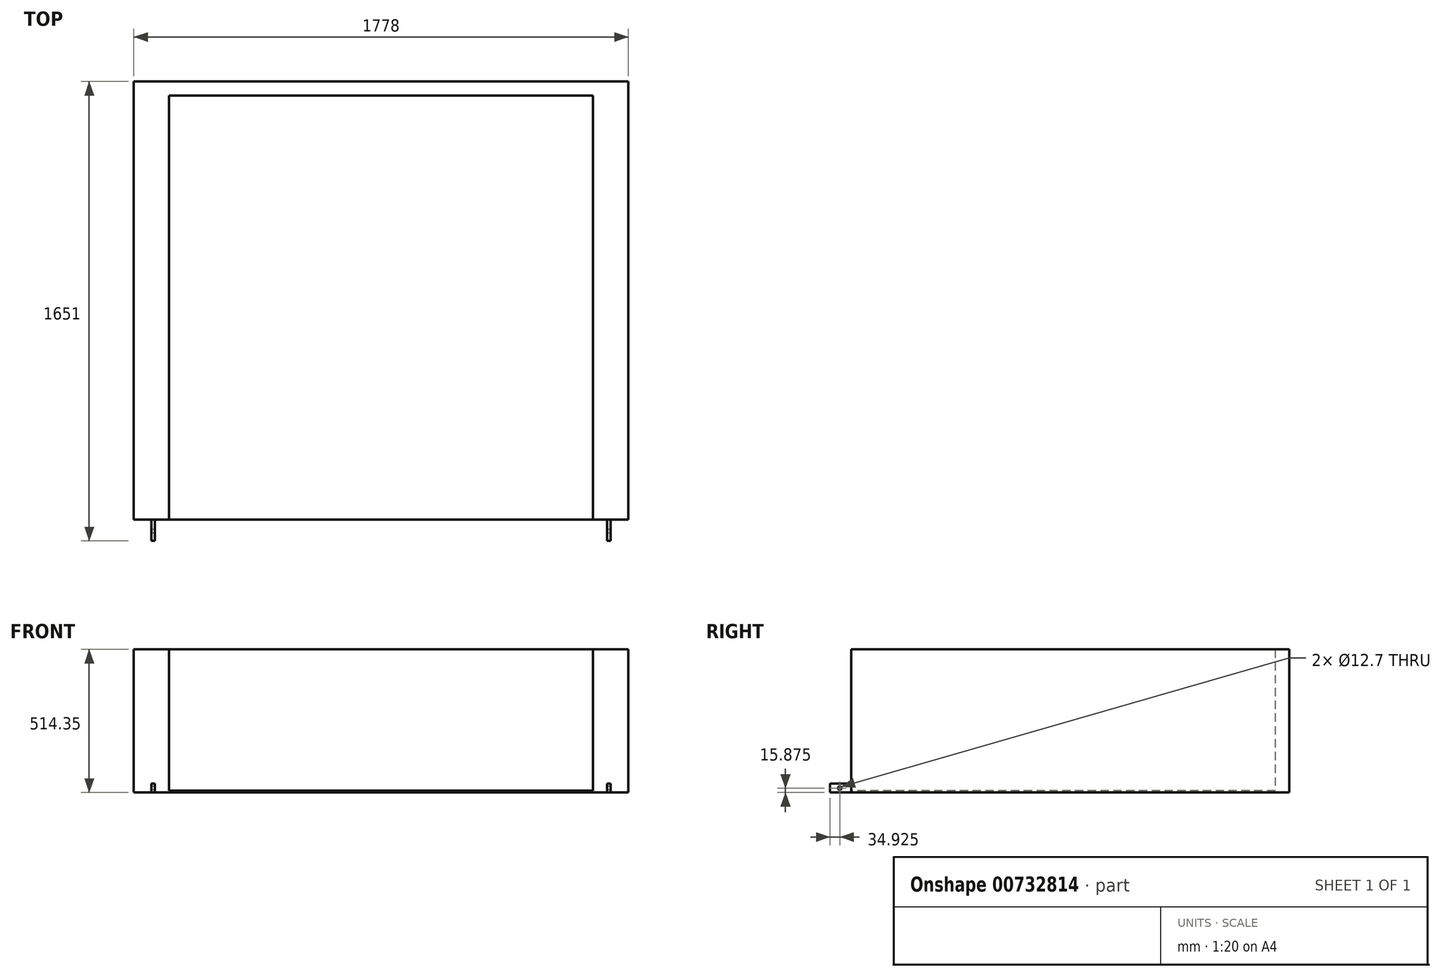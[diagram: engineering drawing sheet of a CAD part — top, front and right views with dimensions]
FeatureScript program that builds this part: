
annotation { "Feature Type Name" : "Feature", "Feature Type Description" : "" }
export const myFeature = defineFeature(function(context is Context, id is Id, definition is map)
    precondition{}
    {
        {
            var Q0;
            Q0=qCreatedBy(makeId("Top.planeOp"),FACE);
            var sketch = newSketch(context, id + "F0", { "sketchPlane" : qUnion([Q0])});
            skLineSegment(sketch, "E0.bottom", {"start": v(-889, 787.4) * mm, "end": v(889, 787.4) * mm});
            skLineSegment(sketch, "E0.top", {"start": v(-889, -787.4) * mm, "end": v(889, -787.4) * mm});
            skLineSegment(sketch, "E0.left", {"start": v(-889, 787.4) * mm, "end": v(-889, -787.4) * mm});
            skLineSegment(sketch, "E0.right", {"start": v(889, 787.4) * mm, "end": v(889, -787.4) * mm});
            skPoint(sketch, "E0.middle", {"position": v(0, 0) * mm});
            skSolve(sketch);
        }
        {
            var Q0;
            Q0 = qSketchRegion(id + "F0", true);
            extrude(context, id + "F1", {"entities" : qUnion([Q0]), "depth" : 6.35 * mm, "offsetDistance" : 25.4 * mm});
        }
        {
            var Q0;
            Q0=makeQuery(id+"F1.opExtrude","CAP_FACE",FACE,{"disambiguationData":[OSD([sQuery(id+"F0.wireOp",EDGE,"E0.bottom"),sQuery(id+"F0.wireOp",EDGE,"E0.top"),sQuery(id+"F0.wireOp",EDGE,"E0.left"),sQuery(id+"F0.wireOp",EDGE,"E0.right")])],"isStart":false});
            var sketch = newSketch(context, id + "F2", { "sketchPlane" : qUnion([Q0])});
            skLineSegment(sketch, "E1.bottom", {"start": v(-889, -787.4) * mm, "end": v(-762, -787.4) * mm});
            skLineSegment(sketch, "E1.top", {"start": v(-889, 787.4) * mm, "end": v(-762, 787.4) * mm});
            skLineSegment(sketch, "E1.left", {"start": v(-889, -787.4) * mm, "end": v(-889, 787.4) * mm});
            skLineSegment(sketch, "E1.right", {"start": v(-762, -787.4) * mm, "end": v(-762, 736.6) * mm});
            skLineSegment(sketch, "E2.bottom", {"start": v(889, 787.4) * mm, "end": v(762, 787.4) * mm});
            skLineSegment(sketch, "E2.top", {"start": v(889, -787.4) * mm, "end": v(762, -787.4) * mm});
            skLineSegment(sketch, "E2.left", {"start": v(889, 787.4) * mm, "end": v(889, -787.4) * mm});
            skLineSegment(sketch, "E2.right", {"start": v(762, 736.6) * mm, "end": v(762, -787.4) * mm});
            skLineSegment(sketch, "E3.bottom", {"start": v(-889, 787.4) * mm, "end": v(889, 787.4) * mm});
            skLineSegment(sketch, "E3.top", {"start": v(-762, 736.6) * mm, "end": v(762, 736.6) * mm});
            skLineSegment(sketch, "E3.left", {"start": v(-889, 787.4) * mm, "end": v(-889, 736.6) * mm});
            skLineSegment(sketch, "E3.right", {"start": v(889, 787.4) * mm, "end": v(889, 736.6) * mm});
            skSolve(sketch);
        }
        {
            var Q0;
            Q0 = qSketchRegion(id + "F2", true);
            extrude(context, id + "F3", {"entities" : qUnion([Q0]), "operationType" : NewBodyOperationType.ADD, "depth" : 508 * mm, "offsetDistance" : 25.4 * mm});
        }
        {
            var Q0;
            Q0=makeQuery(id+"F3.boolean.opBoolean","MERGE",FACE,{"derivedFrom":[makeQuery(id+"F1.opExtrude","SWEPT_FACE",FACE,{"disambiguationData":[OSD([sQuery(id+"F0.wireOp",EDGE,"E0.top")])]}),makeQuery(id+"F3.opExtrude","SWEPT_FACE",FACE,{"disambiguationData":[OSD([sQuery(id+"F2.wireOp",EDGE,"E1.bottom")])]}),makeQuery(id+"F3.opExtrude","SWEPT_FACE",FACE,{"disambiguationData":[OSD([sQuery(id+"F2.wireOp",EDGE,"E2.top")])]})]});
            var sketch = newSketch(context, id + "F4", { "sketchPlane" : qUnion([Q0])});
            skLineSegment(sketch, "E4.bottom", {"start": v(-812.8, 0) * mm, "end": v(-825.5, 0) * mm});
            skLineSegment(sketch, "E4.top", {"start": v(-812.8, 31.75) * mm, "end": v(-825.5, 31.75) * mm});
            skLineSegment(sketch, "E4.left", {"start": v(-812.8, 0) * mm, "end": v(-812.8, 31.75) * mm});
            skLineSegment(sketch, "E4.right", {"start": v(-825.5, 0) * mm, "end": v(-825.5, 31.75) * mm});
            skLineSegment(sketch, "E5.bottom", {"start": v(812.8, 0) * mm, "end": v(825.5, 0) * mm});
            skLineSegment(sketch, "E5.top", {"start": v(812.8, 31.75) * mm, "end": v(825.5, 31.75) * mm});
            skLineSegment(sketch, "E5.left", {"start": v(812.8, 0) * mm, "end": v(812.8, 31.75) * mm});
            skLineSegment(sketch, "E5.right", {"start": v(825.5, 0) * mm, "end": v(825.5, 31.75) * mm});
            skSolve(sketch);
        }
        {
            var Q0;
            Q0 = qSketchRegion(id + "F4", true);
            extrude(context, id + "F5", {"entities" : qUnion([Q0]), "operationType" : NewBodyOperationType.ADD, "depth" : 76.2 * mm, "offsetDistance" : 25.4 * mm});
        }
        {
            var Q0;
            Q0=makeQuery(id+"F5.opExtrude","SWEPT_FACE",FACE,{"disambiguationData":[OSD([sQuery(id+"F4.wireOp",EDGE,"E4.right")])]});
            var sketch = newSketch(context, id + "F6", { "sketchPlane" : qUnion([Q0])});
            skCircle(sketch, "E6", {"center": v(828.68, 15.88) * mm, "radius": 6.35 * mm});
            skSolve(sketch);
        }
        {
            var Q0;
            Q0 = qSketchRegion(id + "F6", true);
            extrude(context, id + "F7", {"entities" : qUnion([Q0]), "operationType" : NewBodyOperationType.REMOVE, "endBound" : BoundingType.THROUGH_ALL, "oppositeDirection" : true, "depth" : 25.4 * mm, "offsetDistance" : 25.4 * mm});
        }
    });
